# Revit family: BC_Aircalo_Fun120-I-droite_LOD400_
name_source: partatom
category: Equipement de génie climatique
revit_build: Autodesk Revit 2017 (Build: 20160225_1515(x64)
units: mm (PartAtom-declared; Revit-internal decimal feet)

## family parameters
Basée sur le plan de construction = Non
Cote de connecteur circulaire = Utiliser le diamètre
Couper avec des vides une fois chargée = Non
Numéro OmniClass = 23.75.70.17.27
Partagée = Non
Point de calcul de pièce = Non
Titre OmniClass = Fan Coil Units
Toujours verticalement = Non
Type d'élément = Normal

## types (2) — shared parameters
Body Material = Body Material
Connection Diameter = 20 mm
Exhaust air diameter = 200 mm
Fabricant = Aircalo
Galvenized Material = Galvanized
Insulation Material = Polyurethane foam fireproof
Main Material = Galvanized steel
Modèle = Ventilo-convecteur gainable FUN 120
Motor power absorbed = 245 W
New Air Diameter = 200 mm
New Air Radius = 63 mm
Nominal Voltage = 230 V
Outlet Diameter = 16 mm
Overall Length = 870 mm
Overall Width = 1465 mm
Power Material = Power Material
Second Diameter = 13 mm
Service Area Material = Service Area

## per-type parameters (varying)
| type | CALC_Height_Consat | Mass | Overall Height |
| FUN 120 I Std - Servitude Droite | 104 mm | 61.00 kg | 237 mm |
| FUN 120 I MCP - Servitude Droite | 96 mm | 62.00 kg | 253 mm |

note: column(s) folded — value = type name in every type: Commentaires du type

## geometry (parser evidence)
native form markers: Sweep x4
no freeform markers — native parametric forms only
